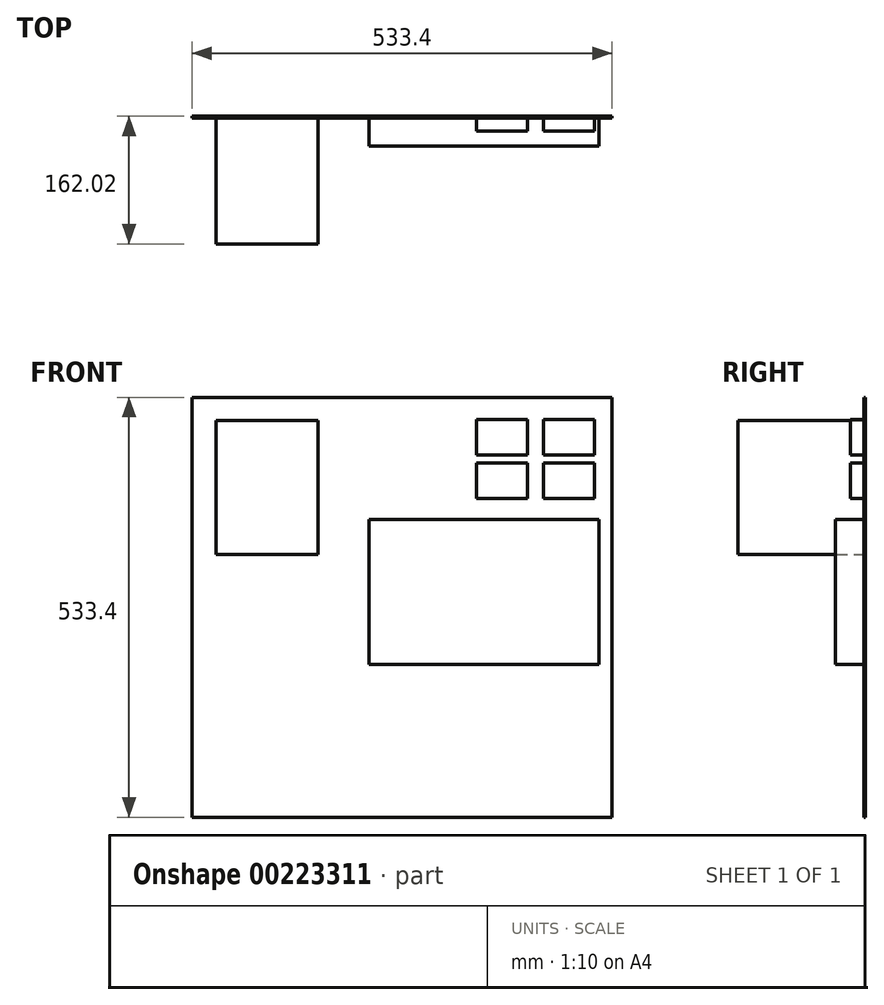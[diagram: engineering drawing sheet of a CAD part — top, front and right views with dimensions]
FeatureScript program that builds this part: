
annotation { "Feature Type Name" : "Feature", "Feature Type Description" : "" }
export const myFeature = defineFeature(function(context is Context, id is Id, definition is map)
    precondition{}
    {
        {
            var Q0;
            Q0=qCreatedBy(makeId("Front.planeOp"),FACE);
            var sketch = newSketch(context, id + "F0", { "sketchPlane" : qUnion([Q0])});
            skLineSegment(sketch, "E0.bottom", {"start": v(266.7, -266.7) * mm, "end": v(-266.7, -266.7) * mm});
            skLineSegment(sketch, "E0.top", {"start": v(266.7, 266.7) * mm, "end": v(-266.7, 266.7) * mm});
            skLineSegment(sketch, "E0.left", {"start": v(266.7, -266.7) * mm, "end": v(266.7, 266.7) * mm});
            skLineSegment(sketch, "E0.right", {"start": v(-266.7, -266.7) * mm, "end": v(-266.7, 266.7) * mm});
            skPoint(sketch, "E0.middle", {"position": v(0, 0) * mm});
            skSolve(sketch);
        }
        {
            var Q0;
            Q0=makeQuery(id+"F0.imprint","IMPRINT",FACE,{"disambiguationData":[TD([[makeQuery(id+"F0.imprint","IMPRINT",EDGE,{"derivedFrom":sQuery(id+"F0.wireOp",EDGE,"E0.bottom")}),-1.0]])]});
            extrude(context, id + "F1", {"entities" : qUnion([Q0]), "depth" : 2 * mm, "offsetDistance" : 25 * mm});
        }
        {
            var Q0;
            Q0=makeQuery(id+"F1.opExtrude","CAP_FACE",FACE,{"disambiguationData":[OSD([sQuery(id+"F0.wireOp",EDGE,"E0.bottom"),sQuery(id+"F0.wireOp",EDGE,"E0.top"),sQuery(id+"F0.wireOp",EDGE,"E0.left"),sQuery(id+"F0.wireOp",EDGE,"E0.right")])],"isStart":false});
            var sketch = newSketch(context, id + "F2", { "sketchPlane" : qUnion([Q0])});
            skLineSegment(sketch, "E1.bottom", {"start": v(250.4, -72.7) * mm, "end": v(-41.7, -72.7) * mm});
            skLineSegment(sketch, "E1.top", {"start": v(250.4, 111.45) * mm, "end": v(-41.7, 111.45) * mm});
            skLineSegment(sketch, "E1.left", {"start": v(250.4, -72.7) * mm, "end": v(250.4, 111.45) * mm});
            skLineSegment(sketch, "E1.right", {"start": v(-41.7, -72.7) * mm, "end": v(-41.7, 111.45) * mm});
            skPoint(sketch, "E1.middle", {"position": v(104.35, 19.37) * mm});
            skSolve(sketch);
        }
        {
            var Q0;
            Q0=makeQuery(id+"F2.imprint","IMPRINT",FACE,{"disambiguationData":[TD([[makeQuery(id+"F2.imprint","IMPRINT",EDGE,{"derivedFrom":sQuery(id+"F2.wireOp",EDGE,"E1.bottom")}),-1.0]])]});
            extrude(context, id + "F3", {"entities" : qUnion([Q0]), "operationType" : NewBodyOperationType.ADD, "depth" : 35.81 * mm, "offsetDistance" : 25 * mm});
        }
        {
            var Q0;
            Q0=makeQuery(id+"F1.opExtrude","CAP_FACE",FACE,{"disambiguationData":[OSD([sQuery(id+"F0.wireOp",EDGE,"E0.bottom"),sQuery(id+"F0.wireOp",EDGE,"E0.top"),sQuery(id+"F0.wireOp",EDGE,"E0.left"),sQuery(id+"F0.wireOp",EDGE,"E0.right")])],"isStart":false});
            var sketch = newSketch(context, id + "F4", { "sketchPlane" : qUnion([Q0])});
            skPoint(sketch, "E2", {"position": v(127, 215.9) * mm});
            skPoint(sketch, "E3.0.1.0", {"position": v(127, 160.9) * mm});
            skPoint(sketch, "E3.1.0.0", {"position": v(212, 215.9) * mm});
            skPoint(sketch, "E3.1.1.0", {"position": v(212, 160.9) * mm});
            skLineSegment(sketch, "E3.direction1", {"start": v(127, 215.9) * mm, "end": v(212, 215.9) * mm, "construction": true});
            skLineSegment(sketch, "E3.direction2", {"start": v(127, 215.9) * mm, "end": v(127, 160.9) * mm, "construction": true});
            skLineSegment(sketch, "E4.bottom", {"start": v(159.5, 238.4) * mm, "end": v(94.5, 238.4) * mm});
            skLineSegment(sketch, "E4.top", {"start": v(159.5, 193.4) * mm, "end": v(94.5, 193.4) * mm});
            skLineSegment(sketch, "E4.left", {"start": v(159.5, 238.4) * mm, "end": v(159.5, 193.4) * mm});
            skLineSegment(sketch, "E4.right", {"start": v(94.5, 238.4) * mm, "end": v(94.5, 193.4) * mm});
            skLineSegment(sketch, "E5.bottom", {"start": v(159.5, 183.4) * mm, "end": v(94.5, 183.4) * mm});
            skLineSegment(sketch, "E5.top", {"start": v(159.5, 138.4) * mm, "end": v(94.5, 138.4) * mm});
            skLineSegment(sketch, "E5.left", {"start": v(159.5, 183.4) * mm, "end": v(159.5, 138.4) * mm});
            skLineSegment(sketch, "E5.right", {"start": v(94.5, 183.4) * mm, "end": v(94.5, 138.4) * mm});
            skLineSegment(sketch, "E6.bottom", {"start": v(244.5, 238.4) * mm, "end": v(179.5, 238.4) * mm});
            skLineSegment(sketch, "E6.top", {"start": v(244.5, 193.4) * mm, "end": v(179.5, 193.4) * mm});
            skLineSegment(sketch, "E6.left", {"start": v(244.5, 238.4) * mm, "end": v(244.5, 193.4) * mm});
            skLineSegment(sketch, "E6.right", {"start": v(179.5, 238.4) * mm, "end": v(179.5, 193.4) * mm});
            skLineSegment(sketch, "E7.bottom", {"start": v(244.5, 138.4) * mm, "end": v(179.5, 138.4) * mm});
            skLineSegment(sketch, "E7.top", {"start": v(244.5, 183.4) * mm, "end": v(179.5, 183.4) * mm});
            skLineSegment(sketch, "E7.left", {"start": v(244.5, 138.4) * mm, "end": v(244.5, 183.4) * mm});
            skLineSegment(sketch, "E7.right", {"start": v(179.5, 138.4) * mm, "end": v(179.5, 183.4) * mm});
            skSolve(sketch);
        }
        {
            var Q0;
            Q0=makeQuery(id+"F4.imprint","IMPRINT",FACE,{"disambiguationData":[TD([[makeQuery(id+"F4.imprint","IMPRINT",EDGE,{"derivedFrom":sQuery(id+"F4.wireOp",EDGE,"E4.bottom")}),1.0]])]});
            var Q1;
            Q1=makeQuery(id+"F4.imprint","IMPRINT",FACE,{"disambiguationData":[TD([[makeQuery(id+"F4.imprint","IMPRINT",EDGE,{"derivedFrom":sQuery(id+"F4.wireOp",EDGE,"E5.bottom")}),1.0]])]});
            var Q2;
            Q2=makeQuery(id+"F4.imprint","IMPRINT",FACE,{"disambiguationData":[TD([[makeQuery(id+"F4.imprint","IMPRINT",EDGE,{"derivedFrom":sQuery(id+"F4.wireOp",EDGE,"E7.bottom")}),-1.0]])]});
            var Q3;
            Q3=makeQuery(id+"F4.imprint","IMPRINT",FACE,{"disambiguationData":[TD([[makeQuery(id+"F4.imprint","IMPRINT",EDGE,{"derivedFrom":sQuery(id+"F4.wireOp",EDGE,"E6.bottom")}),1.0]])]});
            extrude(context, id + "F5", {"entities" : qUnion([Q0, Q1, Q2, Q3]), "operationType" : NewBodyOperationType.ADD, "depth" : 17 * mm, "offsetDistance" : 25 * mm});
        }
        {
            var Q0;
            Q0=makeQuery(id+"F1.opExtrude","CAP_FACE",FACE,{"disambiguationData":[OSD([sQuery(id+"F0.wireOp",EDGE,"E0.bottom"),sQuery(id+"F0.wireOp",EDGE,"E0.top"),sQuery(id+"F0.wireOp",EDGE,"E0.left"),sQuery(id+"F0.wireOp",EDGE,"E0.right")])],"isStart":false});
            var sketch = newSketch(context, id + "F6", { "sketchPlane" : qUnion([Q0])});
            skPoint(sketch, "E8", {"position": v(-171.45, 152.4) * mm});
            skLineSegment(sketch, "E9.bottom", {"start": v(-106.68, 237.5) * mm, "end": v(-236.22, 237.5) * mm});
            skLineSegment(sketch, "E9.top", {"start": v(-106.68, 67.31) * mm, "end": v(-236.22, 67.31) * mm});
            skLineSegment(sketch, "E9.left", {"start": v(-106.68, 237.5) * mm, "end": v(-106.68, 67.31) * mm});
            skLineSegment(sketch, "E9.right", {"start": v(-236.22, 237.5) * mm, "end": v(-236.22, 67.31) * mm});
            skSolve(sketch);
        }
        {
            var Q0;
            Q0=makeQuery(id+"F6.imprint","IMPRINT",FACE,{"disambiguationData":[TD([[makeQuery(id+"F6.imprint","IMPRINT",EDGE,{"derivedFrom":sQuery(id+"F6.wireOp",EDGE,"E9.bottom")}),1.0]])]});
            extrude(context, id + "F7", {"entities" : qUnion([Q0]), "operationType" : NewBodyOperationType.ADD, "depth" : 160.02 * mm, "offsetDistance" : 25 * mm});
        }
    });
